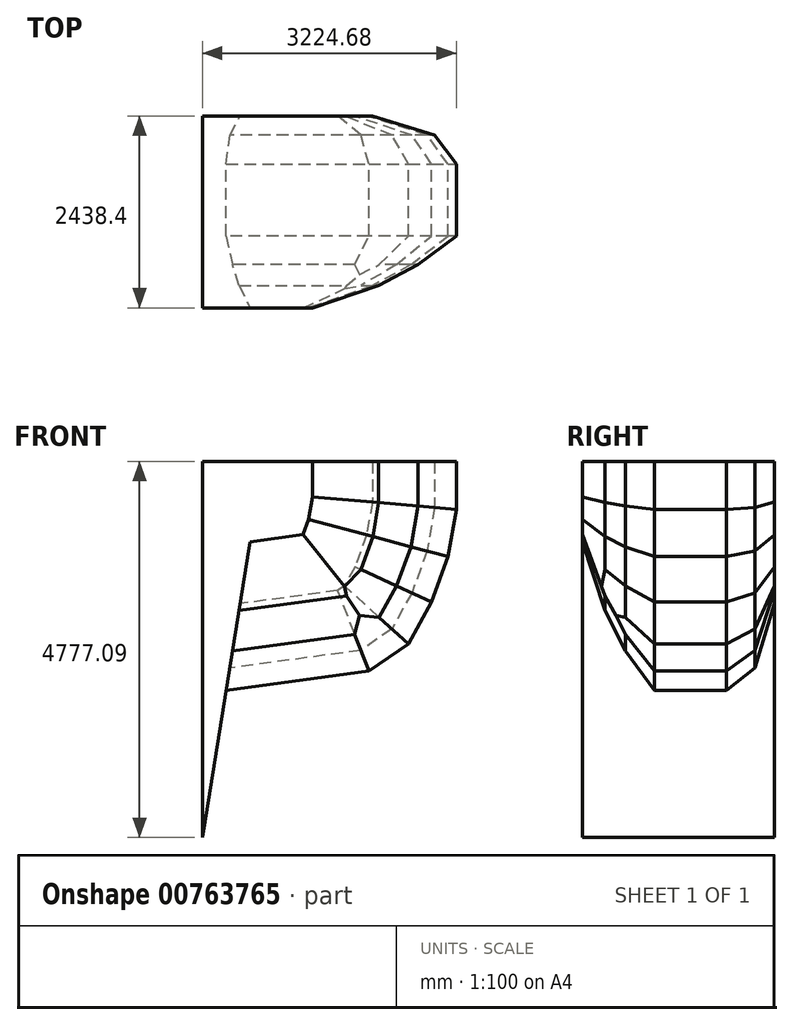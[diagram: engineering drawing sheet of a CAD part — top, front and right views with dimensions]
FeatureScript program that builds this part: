
annotation { "Feature Type Name" : "Feature", "Feature Type Description" : "" }
export const myFeature = defineFeature(function(context is Context, id is Id, definition is map)
    precondition{}
    {
        {
            var Q0;
            Q0=qCreatedBy(makeId("Front.planeOp"),FACE);
            var sketch = newSketch(context, id + "F0", { "sketchPlane" : qUnion([Q0])});
            skLineSegment(sketch, "E0", {"start": v(0, 0) * mm, "end": v(2114.38, 285.73) * mm});
            skLineSegment(sketch, "E1", {"start": v(2114.38, 285.73) * mm, "end": v(2616.24, 631.78) * mm});
            skLineSegment(sketch, "E2", {"start": v(2616.24, 631.78) * mm, "end": v(2911.29, 1165.22) * mm});
            skLineSegment(sketch, "E3", {"start": v(2911.29, 1165.22) * mm, "end": v(3119.14, 1738.3) * mm});
            skLineSegment(sketch, "E4", {"start": v(3119.14, 1738.3) * mm, "end": v(3224.68, 2338.69) * mm});
            skLineSegment(sketch, "E5", {"start": v(3224.68, 2338.69) * mm, "end": v(3224.68, 2948.29) * mm});
            skLineSegment(sketch, "E6", {"start": v(3224.68, 2948.29) * mm, "end": v(0, 2948.29) * mm});
            skLineSegment(sketch, "E7", {"start": v(0, 2948.29) * mm, "end": v(0, 0) * mm});
            skLineSegment(sketch, "E8", {"start": v(0, 0) * mm, "end": v(0, -1828.8) * mm});
            skLineSegment(sketch, "E9", {"start": v(0, 0) * mm, "end": v(302.05, 40.82) * mm});
            skLineSegment(sketch, "E10", {"start": v(302.05, 40.82) * mm, "end": v(0, -1828.8) * mm});
            skSolve(sketch);
        }
        {
            var Q0;
            Q0 = qSketchRegion(id + "F0", true);
            extrude(context, id + "F1", {"entities" : qUnion([Q0]), "depth" : 2438.4 * mm, "offsetDistance" : 25.4 * mm});
        }
        {
            var Q0;
            Q0=makeQuery(id+"F1.opExtrude","CAP_EDGE",EDGE,{"disambiguationData":[OSD([sQuery(id+"F0.wireOp",EDGE,"E5")])],"isStart":false});
            var Q1;
            Q1=makeQuery(id+"F1.opExtrude","CAP_EDGE",EDGE,{"disambiguationData":[OSD([sQuery(id+"F0.wireOp",EDGE,"E4")])],"isStart":false});
            var Q2;
            Q2=makeQuery(id+"F1.opExtrude","CAP_EDGE",EDGE,{"disambiguationData":[OSD([sQuery(id+"F0.wireOp",EDGE,"E3")])],"isStart":false});
            var Q3;
            Q3=makeQuery(id+"F1.opExtrude","CAP_EDGE",EDGE,{"disambiguationData":[OSD([sQuery(id+"F0.wireOp",EDGE,"E2")])],"isStart":false});
            var Q4;
            Q4=makeQuery(id+"F1.opExtrude","CAP_EDGE",EDGE,{"disambiguationData":[OSD([sQuery(id+"F0.wireOp",EDGE,"E1")])],"isStart":false});
            var Q5;
            Q5=makeQuery(id+"F1.opExtrude","CAP_EDGE",EDGE,{"disambiguationData":[OSD([sQuery(id+"F0.wireOp",EDGE,"E0")])],"isStart":false});
            chamfer(context, id + "F2", {"entities" : qUnion([Q0, Q1, Q2, Q3, Q4, Q5]), "chamferType" : ChamferType.TWO_OFFSETS, "width1" : 1219.2 * mm, "oppositeDirection" : false, "width2" : 914.4 * mm, "tangentPropagation" : true});
        }
        {
            var Q0;
            {var subQ0=sQuery(id+"F0.wireOp",EDGE,"E0");Q0=makeQuery(id+"F2.opChamfer","BLEND_EDGE",EDGE,{"blendedFrom":[makeQuery(id+"F1.opExtrude","CAP_EDGE",EDGE,{"disambiguationData":[OSD([subQ0])],"isStart":false}),makeQuery(id+"F1.opExtrude","CAP_FACE",FACE,{"disambiguationData":[OSD([subQ0,sQuery(id+"F0.wireOp",EDGE,"E1"),sQuery(id+"F0.wireOp",EDGE,"E2"),sQuery(id+"F0.wireOp",EDGE,"E3"),sQuery(id+"F0.wireOp",EDGE,"E4"),sQuery(id+"F0.wireOp",EDGE,"E5"),sQuery(id+"F0.wireOp",EDGE,"E6"),sQuery(id+"F0.wireOp",EDGE,"E7"),sQuery(id+"F0.wireOp",EDGE,"E8"),sQuery(id+"F0.wireOp",EDGE,"E10")])],"isStart":false})],"blendedInto":[makeQuery(id+"F1.opExtrude","CAP_FACE",FACE,{"disambiguationData":[OSD([subQ0,sQuery(id+"F0.wireOp",EDGE,"E1"),sQuery(id+"F0.wireOp",EDGE,"E2"),sQuery(id+"F0.wireOp",EDGE,"E3"),sQuery(id+"F0.wireOp",EDGE,"E4"),sQuery(id+"F0.wireOp",EDGE,"E5"),sQuery(id+"F0.wireOp",EDGE,"E6"),sQuery(id+"F0.wireOp",EDGE,"E7"),sQuery(id+"F0.wireOp",EDGE,"E8"),sQuery(id+"F0.wireOp",EDGE,"E10")])],"isStart":false})]});}
            var Q1;
            {var subQ0=sQuery(id+"F0.wireOp",EDGE,"E2");Q1=makeQuery(id+"F2.opChamfer","BLEND_EDGE",EDGE,{"blendedFrom":[makeQuery(id+"F1.opExtrude","CAP_EDGE",EDGE,{"disambiguationData":[OSD([subQ0])],"isStart":false}),makeQuery(id+"F1.opExtrude","CAP_FACE",FACE,{"disambiguationData":[OSD([sQuery(id+"F0.wireOp",EDGE,"E0"),sQuery(id+"F0.wireOp",EDGE,"E1"),subQ0,sQuery(id+"F0.wireOp",EDGE,"E3"),sQuery(id+"F0.wireOp",EDGE,"E4"),sQuery(id+"F0.wireOp",EDGE,"E5"),sQuery(id+"F0.wireOp",EDGE,"E6"),sQuery(id+"F0.wireOp",EDGE,"E7"),sQuery(id+"F0.wireOp",EDGE,"E8"),sQuery(id+"F0.wireOp",EDGE,"E10")])],"isStart":false})],"blendedInto":[makeQuery(id+"F1.opExtrude","CAP_FACE",FACE,{"disambiguationData":[OSD([sQuery(id+"F0.wireOp",EDGE,"E0"),sQuery(id+"F0.wireOp",EDGE,"E1"),subQ0,sQuery(id+"F0.wireOp",EDGE,"E3"),sQuery(id+"F0.wireOp",EDGE,"E4"),sQuery(id+"F0.wireOp",EDGE,"E5"),sQuery(id+"F0.wireOp",EDGE,"E6"),sQuery(id+"F0.wireOp",EDGE,"E7"),sQuery(id+"F0.wireOp",EDGE,"E8"),sQuery(id+"F0.wireOp",EDGE,"E10")])],"isStart":false})]});}
            var Q2;
            {var subQ0=sQuery(id+"F0.wireOp",EDGE,"E3");Q2=makeQuery(id+"F2.opChamfer","BLEND_EDGE",EDGE,{"blendedFrom":[makeQuery(id+"F1.opExtrude","CAP_EDGE",EDGE,{"disambiguationData":[OSD([subQ0])],"isStart":false}),makeQuery(id+"F1.opExtrude","CAP_FACE",FACE,{"disambiguationData":[OSD([sQuery(id+"F0.wireOp",EDGE,"E0"),sQuery(id+"F0.wireOp",EDGE,"E1"),sQuery(id+"F0.wireOp",EDGE,"E2"),subQ0,sQuery(id+"F0.wireOp",EDGE,"E4"),sQuery(id+"F0.wireOp",EDGE,"E5"),sQuery(id+"F0.wireOp",EDGE,"E6"),sQuery(id+"F0.wireOp",EDGE,"E7"),sQuery(id+"F0.wireOp",EDGE,"E8"),sQuery(id+"F0.wireOp",EDGE,"E10")])],"isStart":false})],"blendedInto":[makeQuery(id+"F1.opExtrude","CAP_FACE",FACE,{"disambiguationData":[OSD([sQuery(id+"F0.wireOp",EDGE,"E0"),sQuery(id+"F0.wireOp",EDGE,"E1"),sQuery(id+"F0.wireOp",EDGE,"E2"),subQ0,sQuery(id+"F0.wireOp",EDGE,"E4"),sQuery(id+"F0.wireOp",EDGE,"E5"),sQuery(id+"F0.wireOp",EDGE,"E6"),sQuery(id+"F0.wireOp",EDGE,"E7"),sQuery(id+"F0.wireOp",EDGE,"E8"),sQuery(id+"F0.wireOp",EDGE,"E10")])],"isStart":false})]});}
            var Q3;
            {var subQ0=sQuery(id+"F0.wireOp",EDGE,"E4");Q3=makeQuery(id+"F2.opChamfer","BLEND_EDGE",EDGE,{"blendedFrom":[makeQuery(id+"F1.opExtrude","CAP_EDGE",EDGE,{"disambiguationData":[OSD([subQ0])],"isStart":false}),makeQuery(id+"F1.opExtrude","CAP_FACE",FACE,{"disambiguationData":[OSD([sQuery(id+"F0.wireOp",EDGE,"E0"),sQuery(id+"F0.wireOp",EDGE,"E1"),sQuery(id+"F0.wireOp",EDGE,"E2"),sQuery(id+"F0.wireOp",EDGE,"E3"),subQ0,sQuery(id+"F0.wireOp",EDGE,"E5"),sQuery(id+"F0.wireOp",EDGE,"E6"),sQuery(id+"F0.wireOp",EDGE,"E7"),sQuery(id+"F0.wireOp",EDGE,"E8"),sQuery(id+"F0.wireOp",EDGE,"E10")])],"isStart":false})],"blendedInto":[makeQuery(id+"F1.opExtrude","CAP_FACE",FACE,{"disambiguationData":[OSD([sQuery(id+"F0.wireOp",EDGE,"E0"),sQuery(id+"F0.wireOp",EDGE,"E1"),sQuery(id+"F0.wireOp",EDGE,"E2"),sQuery(id+"F0.wireOp",EDGE,"E3"),subQ0,sQuery(id+"F0.wireOp",EDGE,"E5"),sQuery(id+"F0.wireOp",EDGE,"E6"),sQuery(id+"F0.wireOp",EDGE,"E7"),sQuery(id+"F0.wireOp",EDGE,"E8"),sQuery(id+"F0.wireOp",EDGE,"E10")])],"isStart":false})]});}
            var Q4;
            {var subQ0=sQuery(id+"F0.wireOp",EDGE,"E5");Q4=makeQuery(id+"F2.opChamfer","BLEND_EDGE",EDGE,{"blendedFrom":[makeQuery(id+"F1.opExtrude","CAP_EDGE",EDGE,{"disambiguationData":[OSD([subQ0])],"isStart":false}),makeQuery(id+"F1.opExtrude","CAP_FACE",FACE,{"disambiguationData":[OSD([sQuery(id+"F0.wireOp",EDGE,"E0"),sQuery(id+"F0.wireOp",EDGE,"E1"),sQuery(id+"F0.wireOp",EDGE,"E2"),sQuery(id+"F0.wireOp",EDGE,"E3"),sQuery(id+"F0.wireOp",EDGE,"E4"),subQ0,sQuery(id+"F0.wireOp",EDGE,"E6"),sQuery(id+"F0.wireOp",EDGE,"E7"),sQuery(id+"F0.wireOp",EDGE,"E8"),sQuery(id+"F0.wireOp",EDGE,"E10")])],"isStart":false})],"blendedInto":[makeQuery(id+"F1.opExtrude","CAP_FACE",FACE,{"disambiguationData":[OSD([sQuery(id+"F0.wireOp",EDGE,"E0"),sQuery(id+"F0.wireOp",EDGE,"E1"),sQuery(id+"F0.wireOp",EDGE,"E2"),sQuery(id+"F0.wireOp",EDGE,"E3"),sQuery(id+"F0.wireOp",EDGE,"E4"),subQ0,sQuery(id+"F0.wireOp",EDGE,"E6"),sQuery(id+"F0.wireOp",EDGE,"E7"),sQuery(id+"F0.wireOp",EDGE,"E8"),sQuery(id+"F0.wireOp",EDGE,"E10")])],"isStart":false})]});}
            chamfer(context, id + "F3", {"entities" : qUnion([Q0, Q1, Q2, Q3, Q4]), "chamferType" : ChamferType.TWO_OFFSETS, "width1" : 304.8 * mm, "oppositeDirection" : false, "width2" : 914.4 * mm, "tangentPropagation" : true});
        }
        {
            var Q0;
            {var subQ0=sQuery(id+"F0.wireOp",EDGE,"E0");var subQ1=makeQuery(id+"F1.opExtrude","CAP_FACE",FACE,{"disambiguationData":[OSD([subQ0,sQuery(id+"F0.wireOp",EDGE,"E1"),sQuery(id+"F0.wireOp",EDGE,"E2"),sQuery(id+"F0.wireOp",EDGE,"E3"),sQuery(id+"F0.wireOp",EDGE,"E4"),sQuery(id+"F0.wireOp",EDGE,"E5"),sQuery(id+"F0.wireOp",EDGE,"E6"),sQuery(id+"F0.wireOp",EDGE,"E7"),sQuery(id+"F0.wireOp",EDGE,"E8"),sQuery(id+"F0.wireOp",EDGE,"E10")])],"isStart":false});Q0=makeQuery(id+"F3.opChamfer","BLEND_EDGE",EDGE,{"blendedFrom":[makeQuery(id+"F2.opChamfer","BLEND_EDGE",EDGE,{"blendedFrom":[makeQuery(id+"F1.opExtrude","CAP_EDGE",EDGE,{"disambiguationData":[OSD([subQ0])],"isStart":false}),subQ1],"blendedInto":[subQ1]}),subQ1],"blendedInto":[subQ1]});}
            var Q1;
            {var subQ0=sQuery(id+"F0.wireOp",EDGE,"E3");var subQ1=makeQuery(id+"F1.opExtrude","CAP_FACE",FACE,{"disambiguationData":[OSD([sQuery(id+"F0.wireOp",EDGE,"E0"),sQuery(id+"F0.wireOp",EDGE,"E1"),sQuery(id+"F0.wireOp",EDGE,"E2"),subQ0,sQuery(id+"F0.wireOp",EDGE,"E4"),sQuery(id+"F0.wireOp",EDGE,"E5"),sQuery(id+"F0.wireOp",EDGE,"E6"),sQuery(id+"F0.wireOp",EDGE,"E7"),sQuery(id+"F0.wireOp",EDGE,"E8"),sQuery(id+"F0.wireOp",EDGE,"E10")])],"isStart":false});Q1=makeQuery(id+"F3.opChamfer","BLEND_EDGE",EDGE,{"blendedFrom":[makeQuery(id+"F2.opChamfer","BLEND_EDGE",EDGE,{"blendedFrom":[makeQuery(id+"F1.opExtrude","CAP_EDGE",EDGE,{"disambiguationData":[OSD([subQ0])],"isStart":false}),subQ1],"blendedInto":[subQ1]}),subQ1],"blendedInto":[subQ1]});}
            var Q2;
            {var subQ0=sQuery(id+"F0.wireOp",EDGE,"E4");var subQ1=makeQuery(id+"F1.opExtrude","CAP_FACE",FACE,{"disambiguationData":[OSD([sQuery(id+"F0.wireOp",EDGE,"E0"),sQuery(id+"F0.wireOp",EDGE,"E1"),sQuery(id+"F0.wireOp",EDGE,"E2"),sQuery(id+"F0.wireOp",EDGE,"E3"),subQ0,sQuery(id+"F0.wireOp",EDGE,"E5"),sQuery(id+"F0.wireOp",EDGE,"E6"),sQuery(id+"F0.wireOp",EDGE,"E7"),sQuery(id+"F0.wireOp",EDGE,"E8"),sQuery(id+"F0.wireOp",EDGE,"E10")])],"isStart":false});Q2=makeQuery(id+"F3.opChamfer","BLEND_EDGE",EDGE,{"blendedFrom":[makeQuery(id+"F2.opChamfer","BLEND_EDGE",EDGE,{"blendedFrom":[makeQuery(id+"F1.opExtrude","CAP_EDGE",EDGE,{"disambiguationData":[OSD([subQ0])],"isStart":false}),subQ1],"blendedInto":[subQ1]}),subQ1],"blendedInto":[subQ1]});}
            var Q3;
            {var subQ0=sQuery(id+"F0.wireOp",EDGE,"E5");var subQ1=makeQuery(id+"F1.opExtrude","CAP_FACE",FACE,{"disambiguationData":[OSD([sQuery(id+"F0.wireOp",EDGE,"E0"),sQuery(id+"F0.wireOp",EDGE,"E1"),sQuery(id+"F0.wireOp",EDGE,"E2"),sQuery(id+"F0.wireOp",EDGE,"E3"),sQuery(id+"F0.wireOp",EDGE,"E4"),subQ0,sQuery(id+"F0.wireOp",EDGE,"E6"),sQuery(id+"F0.wireOp",EDGE,"E7"),sQuery(id+"F0.wireOp",EDGE,"E8"),sQuery(id+"F0.wireOp",EDGE,"E10")])],"isStart":false});Q3=makeQuery(id+"F3.opChamfer","BLEND_EDGE",EDGE,{"blendedFrom":[makeQuery(id+"F2.opChamfer","BLEND_EDGE",EDGE,{"blendedFrom":[makeQuery(id+"F1.opExtrude","CAP_EDGE",EDGE,{"disambiguationData":[OSD([subQ0])],"isStart":false}),subQ1],"blendedInto":[subQ1]}),subQ1],"blendedInto":[subQ1]});}
            chamfer(context, id + "F4", {"entities" : qUnion([Q0, Q1, Q2, Q3]), "chamferType" : ChamferType.TWO_OFFSETS, "width1" : 304.8 * mm, "oppositeDirection" : false, "width2" : 609.6 * mm, "tangentPropagation" : true});
        }
        {
            var Q0;
            Q0=makeQuery(id+"F1.opExtrude","CAP_EDGE",EDGE,{"disambiguationData":[OSD([sQuery(id+"F0.wireOp",EDGE,"E5")])],"isStart":true});
            var Q1;
            Q1=makeQuery(id+"F1.opExtrude","CAP_EDGE",EDGE,{"disambiguationData":[OSD([sQuery(id+"F0.wireOp",EDGE,"E4")])],"isStart":true});
            var Q2;
            Q2=makeQuery(id+"F1.opExtrude","CAP_EDGE",EDGE,{"disambiguationData":[OSD([sQuery(id+"F0.wireOp",EDGE,"E3")])],"isStart":true});
            var Q3;
            Q3=makeQuery(id+"F1.opExtrude","CAP_EDGE",EDGE,{"disambiguationData":[OSD([sQuery(id+"F0.wireOp",EDGE,"E2")])],"isStart":true});
            var Q4;
            Q4=makeQuery(id+"F1.opExtrude","CAP_EDGE",EDGE,{"disambiguationData":[OSD([sQuery(id+"F0.wireOp",EDGE,"E1")])],"isStart":true});
            var Q5;
            Q5=makeQuery(id+"F1.opExtrude","CAP_EDGE",EDGE,{"disambiguationData":[OSD([sQuery(id+"F0.wireOp",EDGE,"E0")])],"isStart":true});
            chamfer(context, id + "F5", {"entities" : qUnion([Q0, Q1, Q2, Q3, Q4, Q5]), "chamferType" : ChamferType.TWO_OFFSETS, "width1" : 609.6 * mm, "oppositeDirection" : false, "width2" : 457.2 * mm, "tangentPropagation" : true});
        }
        {
            var Q0;
            {var subQ0=sQuery(id+"F0.wireOp",EDGE,"E5");Q0=makeQuery(id+"F5.opChamfer","BLEND_EDGE",EDGE,{"blendedFrom":[makeQuery(id+"F1.opExtrude","CAP_EDGE",EDGE,{"disambiguationData":[OSD([subQ0])],"isStart":true}),makeQuery(id+"F1.opExtrude","CAP_FACE",FACE,{"disambiguationData":[OSD([sQuery(id+"F0.wireOp",EDGE,"E0"),sQuery(id+"F0.wireOp",EDGE,"E1"),sQuery(id+"F0.wireOp",EDGE,"E2"),sQuery(id+"F0.wireOp",EDGE,"E3"),sQuery(id+"F0.wireOp",EDGE,"E4"),subQ0,sQuery(id+"F0.wireOp",EDGE,"E6"),sQuery(id+"F0.wireOp",EDGE,"E7"),sQuery(id+"F0.wireOp",EDGE,"E8"),sQuery(id+"F0.wireOp",EDGE,"E10")])],"isStart":true})],"blendedInto":[makeQuery(id+"F1.opExtrude","CAP_FACE",FACE,{"disambiguationData":[OSD([sQuery(id+"F0.wireOp",EDGE,"E0"),sQuery(id+"F0.wireOp",EDGE,"E1"),sQuery(id+"F0.wireOp",EDGE,"E2"),sQuery(id+"F0.wireOp",EDGE,"E3"),sQuery(id+"F0.wireOp",EDGE,"E4"),subQ0,sQuery(id+"F0.wireOp",EDGE,"E6"),sQuery(id+"F0.wireOp",EDGE,"E7"),sQuery(id+"F0.wireOp",EDGE,"E8"),sQuery(id+"F0.wireOp",EDGE,"E10")])],"isStart":true})]});}
            var Q1;
            {var subQ0=sQuery(id+"F0.wireOp",EDGE,"E4");Q1=makeQuery(id+"F5.opChamfer","BLEND_EDGE",EDGE,{"blendedFrom":[makeQuery(id+"F1.opExtrude","CAP_EDGE",EDGE,{"disambiguationData":[OSD([subQ0])],"isStart":true}),makeQuery(id+"F1.opExtrude","CAP_FACE",FACE,{"disambiguationData":[OSD([sQuery(id+"F0.wireOp",EDGE,"E0"),sQuery(id+"F0.wireOp",EDGE,"E1"),sQuery(id+"F0.wireOp",EDGE,"E2"),sQuery(id+"F0.wireOp",EDGE,"E3"),subQ0,sQuery(id+"F0.wireOp",EDGE,"E5"),sQuery(id+"F0.wireOp",EDGE,"E6"),sQuery(id+"F0.wireOp",EDGE,"E7"),sQuery(id+"F0.wireOp",EDGE,"E8"),sQuery(id+"F0.wireOp",EDGE,"E10")])],"isStart":true})],"blendedInto":[makeQuery(id+"F1.opExtrude","CAP_FACE",FACE,{"disambiguationData":[OSD([sQuery(id+"F0.wireOp",EDGE,"E0"),sQuery(id+"F0.wireOp",EDGE,"E1"),sQuery(id+"F0.wireOp",EDGE,"E2"),sQuery(id+"F0.wireOp",EDGE,"E3"),subQ0,sQuery(id+"F0.wireOp",EDGE,"E5"),sQuery(id+"F0.wireOp",EDGE,"E6"),sQuery(id+"F0.wireOp",EDGE,"E7"),sQuery(id+"F0.wireOp",EDGE,"E8"),sQuery(id+"F0.wireOp",EDGE,"E10")])],"isStart":true})]});}
            var Q2;
            {var subQ0=sQuery(id+"F0.wireOp",EDGE,"E3");Q2=makeQuery(id+"F5.opChamfer","BLEND_EDGE",EDGE,{"blendedFrom":[makeQuery(id+"F1.opExtrude","CAP_EDGE",EDGE,{"disambiguationData":[OSD([subQ0])],"isStart":true}),makeQuery(id+"F1.opExtrude","CAP_FACE",FACE,{"disambiguationData":[OSD([sQuery(id+"F0.wireOp",EDGE,"E0"),sQuery(id+"F0.wireOp",EDGE,"E1"),sQuery(id+"F0.wireOp",EDGE,"E2"),subQ0,sQuery(id+"F0.wireOp",EDGE,"E4"),sQuery(id+"F0.wireOp",EDGE,"E5"),sQuery(id+"F0.wireOp",EDGE,"E6"),sQuery(id+"F0.wireOp",EDGE,"E7"),sQuery(id+"F0.wireOp",EDGE,"E8"),sQuery(id+"F0.wireOp",EDGE,"E10")])],"isStart":true})],"blendedInto":[makeQuery(id+"F1.opExtrude","CAP_FACE",FACE,{"disambiguationData":[OSD([sQuery(id+"F0.wireOp",EDGE,"E0"),sQuery(id+"F0.wireOp",EDGE,"E1"),sQuery(id+"F0.wireOp",EDGE,"E2"),subQ0,sQuery(id+"F0.wireOp",EDGE,"E4"),sQuery(id+"F0.wireOp",EDGE,"E5"),sQuery(id+"F0.wireOp",EDGE,"E6"),sQuery(id+"F0.wireOp",EDGE,"E7"),sQuery(id+"F0.wireOp",EDGE,"E8"),sQuery(id+"F0.wireOp",EDGE,"E10")])],"isStart":true})]});}
            var Q3;
            {var subQ0=sQuery(id+"F0.wireOp",EDGE,"E2");Q3=makeQuery(id+"F5.opChamfer","BLEND_EDGE",EDGE,{"blendedFrom":[makeQuery(id+"F1.opExtrude","CAP_EDGE",EDGE,{"disambiguationData":[OSD([subQ0])],"isStart":true}),makeQuery(id+"F1.opExtrude","CAP_FACE",FACE,{"disambiguationData":[OSD([sQuery(id+"F0.wireOp",EDGE,"E0"),sQuery(id+"F0.wireOp",EDGE,"E1"),subQ0,sQuery(id+"F0.wireOp",EDGE,"E3"),sQuery(id+"F0.wireOp",EDGE,"E4"),sQuery(id+"F0.wireOp",EDGE,"E5"),sQuery(id+"F0.wireOp",EDGE,"E6"),sQuery(id+"F0.wireOp",EDGE,"E7"),sQuery(id+"F0.wireOp",EDGE,"E8"),sQuery(id+"F0.wireOp",EDGE,"E10")])],"isStart":true})],"blendedInto":[makeQuery(id+"F1.opExtrude","CAP_FACE",FACE,{"disambiguationData":[OSD([sQuery(id+"F0.wireOp",EDGE,"E0"),sQuery(id+"F0.wireOp",EDGE,"E1"),subQ0,sQuery(id+"F0.wireOp",EDGE,"E3"),sQuery(id+"F0.wireOp",EDGE,"E4"),sQuery(id+"F0.wireOp",EDGE,"E5"),sQuery(id+"F0.wireOp",EDGE,"E6"),sQuery(id+"F0.wireOp",EDGE,"E7"),sQuery(id+"F0.wireOp",EDGE,"E8"),sQuery(id+"F0.wireOp",EDGE,"E10")])],"isStart":true})]});}
            var Q4;
            {var subQ0=sQuery(id+"F0.wireOp",EDGE,"E1");Q4=makeQuery(id+"F5.opChamfer","BLEND_EDGE",EDGE,{"blendedFrom":[makeQuery(id+"F1.opExtrude","CAP_EDGE",EDGE,{"disambiguationData":[OSD([subQ0])],"isStart":true}),makeQuery(id+"F1.opExtrude","CAP_FACE",FACE,{"disambiguationData":[OSD([sQuery(id+"F0.wireOp",EDGE,"E0"),subQ0,sQuery(id+"F0.wireOp",EDGE,"E2"),sQuery(id+"F0.wireOp",EDGE,"E3"),sQuery(id+"F0.wireOp",EDGE,"E4"),sQuery(id+"F0.wireOp",EDGE,"E5"),sQuery(id+"F0.wireOp",EDGE,"E6"),sQuery(id+"F0.wireOp",EDGE,"E7"),sQuery(id+"F0.wireOp",EDGE,"E8"),sQuery(id+"F0.wireOp",EDGE,"E10")])],"isStart":true})],"blendedInto":[makeQuery(id+"F1.opExtrude","CAP_FACE",FACE,{"disambiguationData":[OSD([sQuery(id+"F0.wireOp",EDGE,"E0"),subQ0,sQuery(id+"F0.wireOp",EDGE,"E2"),sQuery(id+"F0.wireOp",EDGE,"E3"),sQuery(id+"F0.wireOp",EDGE,"E4"),sQuery(id+"F0.wireOp",EDGE,"E5"),sQuery(id+"F0.wireOp",EDGE,"E6"),sQuery(id+"F0.wireOp",EDGE,"E7"),sQuery(id+"F0.wireOp",EDGE,"E8"),sQuery(id+"F0.wireOp",EDGE,"E10")])],"isStart":true})]});}
            var Q5;
            {var subQ0=sQuery(id+"F0.wireOp",EDGE,"E0");Q5=makeQuery(id+"F5.opChamfer","BLEND_EDGE",EDGE,{"blendedFrom":[makeQuery(id+"F1.opExtrude","CAP_EDGE",EDGE,{"disambiguationData":[OSD([subQ0])],"isStart":true}),makeQuery(id+"F1.opExtrude","CAP_FACE",FACE,{"disambiguationData":[OSD([subQ0,sQuery(id+"F0.wireOp",EDGE,"E1"),sQuery(id+"F0.wireOp",EDGE,"E2"),sQuery(id+"F0.wireOp",EDGE,"E3"),sQuery(id+"F0.wireOp",EDGE,"E4"),sQuery(id+"F0.wireOp",EDGE,"E5"),sQuery(id+"F0.wireOp",EDGE,"E6"),sQuery(id+"F0.wireOp",EDGE,"E7"),sQuery(id+"F0.wireOp",EDGE,"E8"),sQuery(id+"F0.wireOp",EDGE,"E10")])],"isStart":true})],"blendedInto":[makeQuery(id+"F1.opExtrude","CAP_FACE",FACE,{"disambiguationData":[OSD([subQ0,sQuery(id+"F0.wireOp",EDGE,"E1"),sQuery(id+"F0.wireOp",EDGE,"E2"),sQuery(id+"F0.wireOp",EDGE,"E3"),sQuery(id+"F0.wireOp",EDGE,"E4"),sQuery(id+"F0.wireOp",EDGE,"E5"),sQuery(id+"F0.wireOp",EDGE,"E6"),sQuery(id+"F0.wireOp",EDGE,"E7"),sQuery(id+"F0.wireOp",EDGE,"E8"),sQuery(id+"F0.wireOp",EDGE,"E10")])],"isStart":true})]});}
            chamfer(context, id + "F6", {"entities" : qUnion([Q0, Q1, Q2, Q3, Q4, Q5]), "chamferType" : ChamferType.TWO_OFFSETS, "width1" : 609.6 * mm, "oppositeDirection" : false, "width2" : 304.8 * mm, "tangentPropagation" : true});
        }
    });
